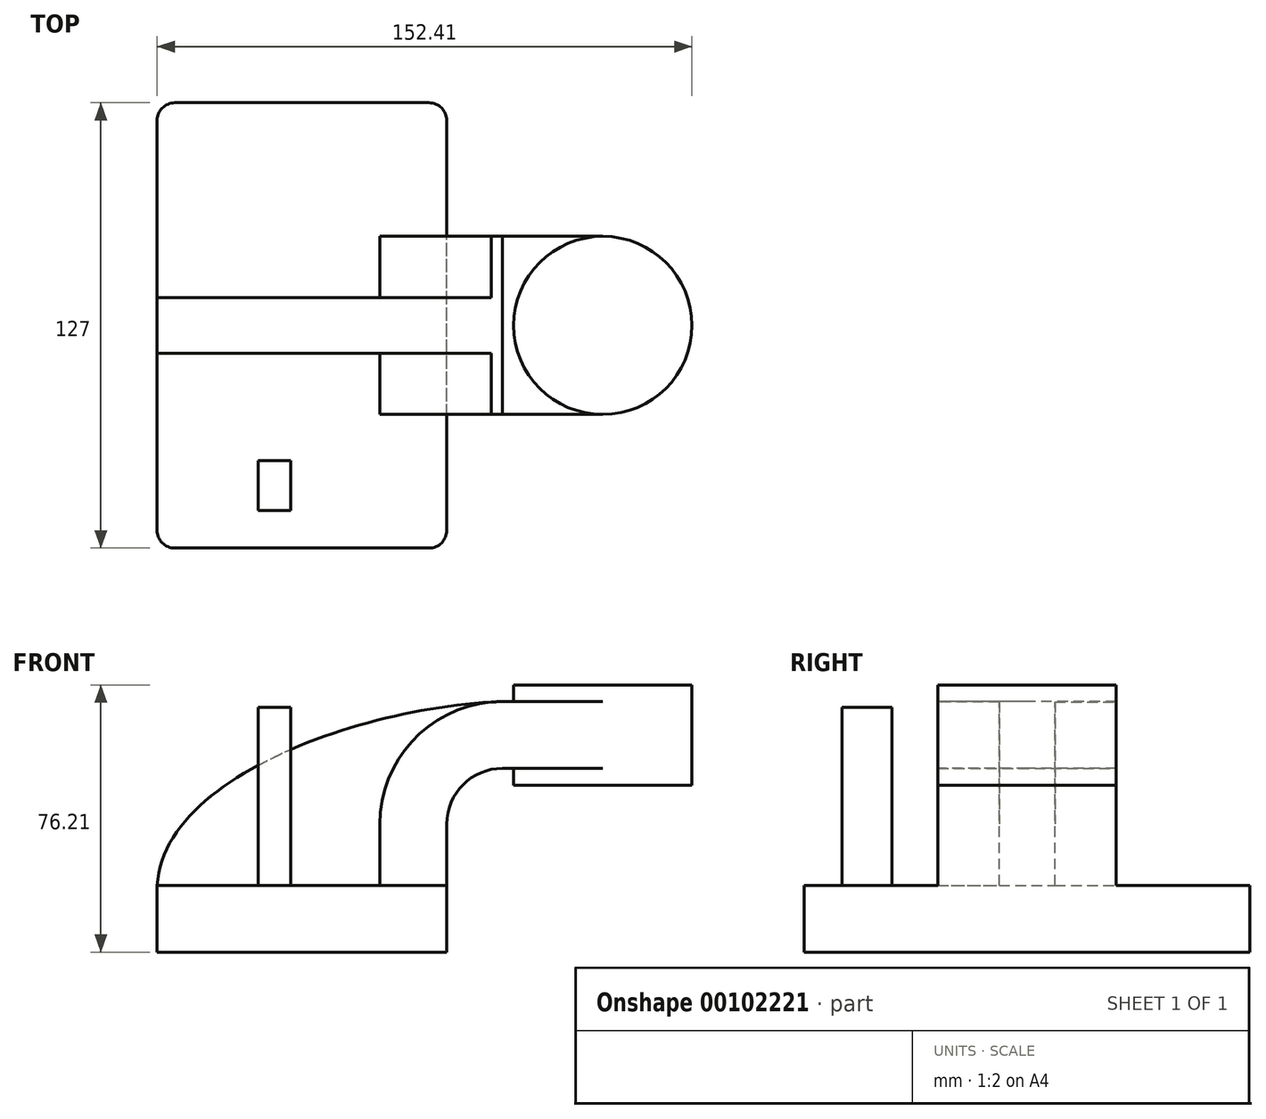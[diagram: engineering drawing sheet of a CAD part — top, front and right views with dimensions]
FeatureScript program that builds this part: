
annotation { "Feature Type Name" : "Feature", "Feature Type Description" : "" }
export const myFeature = defineFeature(function(context is Context, id is Id, definition is map)
    precondition{}
    {
        {
            var Q0;
            Q0=qCreatedBy(makeId("Front.planeOp"),FACE);
            var sketch = newSketch(context, id + "F0", { "sketchPlane" : qUnion([Q0])});
            skLineSegment(sketch, "E0.rect.bottom", {"start": v(-41.28, 9.52) * mm, "end": v(41.28, 9.52) * mm});
            skLineSegment(sketch, "E0.rect.top", {"start": v(-41.28, -9.52) * mm, "end": v(41.28, -9.52) * mm});
            skLineSegment(sketch, "E0.rect.left", {"start": v(-41.28, 9.52) * mm, "end": v(-41.28, -9.52) * mm});
            skLineSegment(sketch, "E0.rect.right", {"start": v(41.28, 9.52) * mm, "end": v(41.28, -9.52) * mm});
            skPoint(sketch, "E0.rect.middle", {"position": v(0, 0) * mm});
            skLineSegment(sketch, "E1", {"start": v(41.28, 9.52) * mm, "end": v(41.28, 27) * mm});
            skArc(sketch, "E2", {"start": v(41.28, 27) * mm, "mid": v(45.92, 38.23) * mm, "end": v(57.15, 42.88) * mm});
            skLineSegment(sketch, "E3", {"start": v(57.15, 42.88) * mm, "end": v(85.72, 42.88) * mm});
            skLineSegment(sketch, "E4.rect.bottom", {"start": v(60.32, 38.1) * mm, "end": v(111.12, 38.1) * mm});
            skLineSegment(sketch, "E4.rect.top", {"start": v(60.32, 66.68) * mm, "end": v(111.12, 66.68) * mm});
            skLineSegment(sketch, "E4.rect.left", {"start": v(60.32, 38.1) * mm, "end": v(60.32, 66.68) * mm});
            skLineSegment(sketch, "E4.rect.right", {"start": v(111.13, 38.1) * mm, "end": v(111.12, 66.68) * mm});
            skPoint(sketch, "E4.rect.middle", {"position": v(85.72, 52.39) * mm});
            skLineSegment(sketch, "E5.0", {"start": v(57.15, 61.93) * mm, "end": v(85.72, 61.93) * mm});
            skArc(sketch, "E5.1", {"start": v(22.23, 27) * mm, "mid": v(32.45, 51.7) * mm, "end": v(57.15, 61.93) * mm});
            skLineSegment(sketch, "E5.2", {"start": v(22.23, 9.52) * mm, "end": v(22.23, 27) * mm});
            skLineSegment(sketch, "E6", {"start": v(85.72, 38.1) * mm, "end": v(85.72, 66.68) * mm});
            skFitSpline(sketch, "E7", {"points": [v(-41.28, 9.53) * mm, v(57.15, 61.93) * mm], "startDerivative": vector(5.2, 92.34) * mm, "endDerivative": vector(120.92, 4.22) * mm});
            skSolve(sketch);
        }
        {
            var Q0;
            Q0=makeQuery(id+"F0.imprint","IMPRINT",FACE,{"disambiguationData":[TD([[makeQuery(id+"F0.imprint","IMPRINT",EDGE,{"derivedFrom":sQuery(id+"F0.wireOp",EDGE,"E0.rect.top")}),1.0]])]});
            extrude(context, id + "F1", {"entities" : qUnion([Q0]), "endBound" : BoundingType.SYMMETRIC, "depth" : 127 * mm});
        }
        {
            var Q0;
            {var subQ9=sQuery(id+"F0.wireOp",EDGE,"E1");Q0=makeQuery(id+"F0.imprint","IMPRINT",FACE,{"disambiguationData":[TD([[makeQuery(id+"F0.imprint","IMPRINT",EDGE,{"derivedFrom":subQ9}),1.0]])]});}
            var Q1;
            {var subQ0=sQuery(id+"F0.wireOp",EDGE,"E6");var subQ1=sQuery(id+"F0.wireOp",EDGE,"E3");var subQ2=makeQuery(id+"F0.imprint","INTERSECT",VERTEX,{"derivedFrom":[subQ1,subQ0]});Q1=makeQuery(id+"F0.imprint","IMPRINT",FACE,{"disambiguationData":[TD([[makeQuery(id+"F0.imprint","IMPRINT",EDGE,{"disambiguationData":[TD([[subQ2,1.0]])],"derivedFrom":subQ1}),1.0]])]});}
            extrude(context, id + "F2", {"entities" : qUnion([Q0, Q1]), "operationType" : NewBodyOperationType.ADD, "endBound" : BoundingType.SYMMETRIC, "depth" : 50.8 * mm});
        }
        {
            var Q0;
            {var subQ3=sQuery(id+"F0.wireOp",EDGE,"E5.2");Q0=makeQuery(id+"F0.imprint","IMPRINT",FACE,{"disambiguationData":[TD([[makeQuery(id+"F0.imprint","IMPRINT",EDGE,{"derivedFrom":subQ3}),1.0]])]});}
            extrude(context, id + "F3", {"entities" : qUnion([Q0]), "operationType" : NewBodyOperationType.ADD, "endBound" : BoundingType.SYMMETRIC, "depth" : 15.88 * mm});
        }
        {
            var Q0;
            {var subQ5=sQuery(id+"F0.wireOp",EDGE,"E4.rect.right");Q0=makeQuery(id+"F0.imprint","IMPRINT",FACE,{"disambiguationData":[TD([[makeQuery(id+"F0.imprint","IMPRINT",EDGE,{"derivedFrom":subQ5}),1.0]])]});}
            var Q1;
            Q1=sQuery(id+"F0.wireOp",EDGE,"E6");
            revolve(context, id + "F4", {"operationType" : NewBodyOperationType.ADD, "entities" : qUnion([Q0]), "axis" : qUnion([Q1]), "revolveType" : RevolveType.FULL});
        }
        {
            var Q0;
            Q0=makeQuery(id+"F1.opExtrude","CAP_EDGE",EDGE,{"disambiguationData":[OSD([sQuery(id+"F0.wireOp",EDGE,"E0.rect.right")])],"isStart":false});
            var Q1;
            Q1=makeQuery(id+"F1.opExtrude","CAP_EDGE",EDGE,{"disambiguationData":[OSD([sQuery(id+"F0.wireOp",EDGE,"E0.rect.left")])],"isStart":false});
            var Q2;
            Q2=makeQuery(id+"F1.opExtrude","CAP_EDGE",EDGE,{"disambiguationData":[OSD([sQuery(id+"F0.wireOp",EDGE,"E0.rect.right")])],"isStart":true});
            var Q3;
            Q3=makeQuery(id+"F1.opExtrude","CAP_EDGE",EDGE,{"disambiguationData":[OSD([sQuery(id+"F0.wireOp",EDGE,"E0.rect.left")])],"isStart":true});
            fillet(context, id + "F5", {"entities" : qUnion([Q0, Q1, Q2, Q3]), "radius" : 5.08 * mm, "tangentPropagation" : true, "allowEdgeOverflow" : false});
        }
        {
            var Q0;
            {var subQ4=sQuery(id+"F0.wireOp",EDGE,"E0.rect.bottom");var subQ5=sQuery(id+"F0.wireOp",EDGE,"E0.rect.right");var subQ6=sQuery(id+"F0.wireOp",EDGE,"E0.rect.left");Q0=makeQuery(id+"F3.boolean.opBoolean","SPLIT",FACE,{"disambiguationData":[TD([makeQuery(id+"F1.opExtrude","CAP_FACE",FACE,{"disambiguationData":[OSD([subQ4,sQuery(id+"F0.wireOp",EDGE,"E0.rect.top"),subQ6,subQ5])],"isStart":false})])],"derivedFrom":makeQuery(id+"F1.opExtrude","SWEPT_FACE",FACE,{"disambiguationData":[OSD([subQ4])]})});}
            var sketch = newSketch(context, id + "F6", { "sketchPlane" : qUnion([Q0])});
            skLineSegment(sketch, "E8.bottom", {"start": v(-12.43, -52.75) * mm, "end": v(-3.21, -52.75) * mm});
            skLineSegment(sketch, "E8.top", {"start": v(-12.43, -38.51) * mm, "end": v(-3.21, -38.51) * mm});
            skLineSegment(sketch, "E8.left", {"start": v(-12.43, -52.75) * mm, "end": v(-12.43, -38.51) * mm});
            skLineSegment(sketch, "E8.right", {"start": v(-3.21, -52.75) * mm, "end": v(-3.21, -38.51) * mm});
            skSolve(sketch);
        }
        {
            var Q0;
            Q0=makeQuery(id+"F6.imprint","IMPRINT",FACE,{"disambiguationData":[TD([[makeQuery(id+"F6.imprint","IMPRINT",EDGE,{"derivedFrom":sQuery(id+"F6.wireOp",EDGE,"E8.bottom")}),1.0]])]});
            extrude(context, id + "F7", {"entities" : qUnion([Q0]), "operationType" : NewBodyOperationType.ADD, "depth" : 50.8 * mm});
        }
    });
